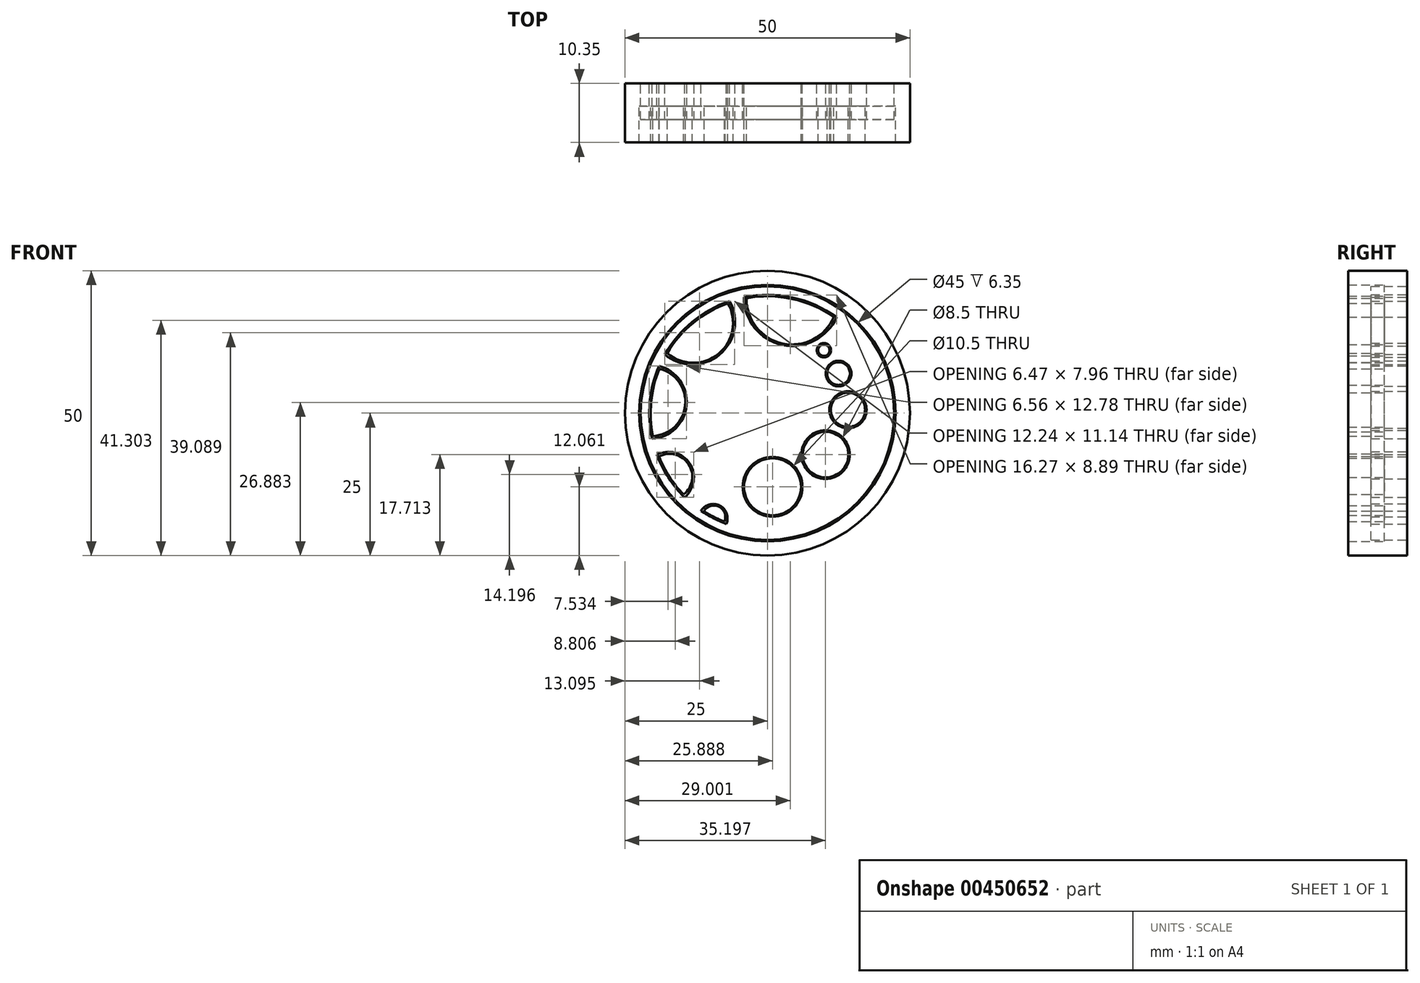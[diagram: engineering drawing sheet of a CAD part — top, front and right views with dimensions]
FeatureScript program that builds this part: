
annotation { "Feature Type Name" : "Feature", "Feature Type Description" : "" }
export const myFeature = defineFeature(function(context is Context, id is Id, definition is map)
    precondition{}
    {
        {
            var Q0;
            Q0=qCreatedBy(makeId("Front.planeOp"),FACE);
            var sketch = newSketch(context, id + "F0", { "sketchPlane" : qUnion([Q0])});
            skCircle(sketch, "E0", {"center": v(0, 0) * mm, "radius": 25 * mm});
            skCircle(sketch, "E1", {"center": v(0, 0) * mm, "radius": 20.5 * mm});
            skText(sketch, "E2", { "text": "BioE 123\n    SM", "fontName": "OpenSans-Bold.ttf"});
            skCircle(sketch, "E3", {"center": v(0.89, -12.94) * mm, "radius": 5 * mm});
            skCircle(sketch, "E4", {"center": v(10.2, -7.29) * mm, "radius": 4 * mm});
            skCircle(sketch, "E5", {"center": v(14.14, 0.57) * mm, "radius": 3 * mm});
            skCircle(sketch, "E6", {"center": v(12.48, 6.93) * mm, "radius": 2 * mm});
            skCircle(sketch, "E7", {"center": v(9.9, 11.03) * mm, "radius": 1 * mm});
            skCircle(sketch, "E8", {"center": v(0, 0) * mm, "radius": 22.5 * mm});
            skArc(sketch, "E9", {"start": v(-14.7, -14.29) * mm, "mid": v(-13.84, -8.99) * mm, "end": v(-19.03, -7.61) * mm});
            skArc(sketch, "E10", {"start": v(-20.1, -4.04) * mm, "mid": v(-14.43, 1.38) * mm, "end": v(-18.97, 7.78) * mm});
            skArc(sketch, "E11", {"start": v(-17.6, 10.52) * mm, "mid": v(-8.58, 10.42) * mm, "end": v(-6.95, 19.29) * mm});
            skArc(sketch, "E12", {"start": v(-3.68, 20.17) * mm, "mid": v(2.63, 12.22) * mm, "end": v(11.66, 16.86) * mm});
            skArc(sketch, "E13", {"start": v(-7.57, -19.05) * mm, "mid": v(-8.47, -16.45) * mm, "end": v(-11.12, -17.22) * mm});
            const initialGuessF0  = {"E2": [-0.01036, 0.0007, 1, 0, 0.00347]};
            skSetInitialGuess(sketch, initialGuessF0);
            skSolve(sketch);
        }
        {
            var Q0;
            Q0=qCreatedBy(makeId("Front.planeOp"),FACE);
            var sketch = newSketch(context, id + "F1", { "sketchPlane" : qUnion([Q0])});
            skCircle(sketch, "E14", {"center": v(0, 0) * mm, "radius": 25 * mm});
            skCircle(sketch, "E15", {"center": v(0, 0) * mm, "radius": 20.75 * mm});
            skText(sketch, "E16", { "text": "BioE 123\n    SM", "fontName": "OpenSans-Bold.ttf"});
            skCircle(sketch, "E17", {"center": v(0.89, -12.94) * mm, "radius": 5.25 * mm});
            skCircle(sketch, "E18", {"center": v(10.2, -7.29) * mm, "radius": 4.25 * mm});
            skCircle(sketch, "E19", {"center": v(14.14, 0.57) * mm, "radius": 3.25 * mm});
            skCircle(sketch, "E20", {"center": v(12.48, 6.93) * mm, "radius": 2.25 * mm});
            skCircle(sketch, "E21", {"center": v(9.9, 11.03) * mm, "radius": 1.25 * mm});
            skCircle(sketch, "E22", {"center": v(0, 0) * mm, "radius": 22.25 * mm});
            skArc(sketch, "E23", {"start": v(-14.56, -14.79) * mm, "mid": v(-13.63, -8.85) * mm, "end": v(-19.43, -7.28) * mm});
            skArc(sketch, "E24", {"start": v(-20.25, -4.5) * mm, "mid": v(-14.18, 1.36) * mm, "end": v(-19.03, 8.27) * mm});
            skArc(sketch, "E25", {"start": v(-18.02, 10.28) * mm, "mid": v(-8.42, 10.23) * mm, "end": v(-6.64, 19.66) * mm});
            skArc(sketch, "E26", {"start": v(-4.13, 20.33) * mm, "mid": v(2.58, 11.98) * mm, "end": v(12.13, 16.83) * mm});
            skArc(sketch, "E27", {"start": v(-7.22, -19.46) * mm, "mid": v(-8.36, -16.22) * mm, "end": v(-11.65, -17.17) * mm});
            const initialGuessF1  = {"E16": [-0.01036, 0.0007, 1, 0, 0.00347]};
            skSetInitialGuess(sketch, initialGuessF1);
            skSolve(sketch);
        }
        {
            var Q0;
            Q0=makeQuery(id+"F0.imprint","IMPRINT",FACE,{"disambiguationData":[TD([[makeQuery(id+"F0.imprint","IMPRINT",EDGE,{"derivedFrom":sQuery(id+"F0.wireOp",EDGE,"E6")}),1.0]])]});
            var Q1;
            Q1=makeQuery(id+"F0.imprint","IMPRINT",FACE,{"disambiguationData":[TD([[makeQuery(id+"F0.imprint","IMPRINT",EDGE,{"derivedFrom":sQuery(id+"F0.wireOp",EDGE,"E5")}),1.0]])]});
            var Q2;
            Q2=makeQuery(id+"F0.imprint","IMPRINT",FACE,{"disambiguationData":[TD([[makeQuery(id+"F0.imprint","IMPRINT",EDGE,{"derivedFrom":sQuery(id+"F0.wireOp",EDGE,"E4")}),1.0]])]});
            var Q3;
            Q3=makeQuery(id+"F0.imprint","IMPRINT",FACE,{"disambiguationData":[TD([[makeQuery(id+"F0.imprint","IMPRINT",EDGE,{"derivedFrom":sQuery(id+"F0.wireOp",EDGE,"E3")}),1.0]])]});
            var Q4;
            Q4=makeQuery(id+"F0.imprint","IMPRINT",FACE,{"disambiguationData":[TD([[makeQuery(id+"F0.imprint","IMPRINT",EDGE,{"derivedFrom":sQuery(id+"F0.wireOp",EDGE,"E2.sketch_text.stroke-0")}),1.0]])]});
            var Q5;
            Q5=makeQuery(id+"F0.imprint","IMPRINT",FACE,{"disambiguationData":[TD([[makeQuery(id+"F0.imprint","IMPRINT",EDGE,{"derivedFrom":sQuery(id+"F0.wireOp",EDGE,"E8")}),1.0]])]});
            var Q6;
            Q6=makeQuery(id+"F0.imprint","IMPRINT",FACE,{"disambiguationData":[TD([[makeQuery(id+"F0.imprint","IMPRINT",EDGE,{"derivedFrom":sQuery(id+"F0.wireOp",EDGE,"E0")}),1.0]])]});
            var Q7;
            {var subQ0=sQuery(id+"F0.wireOp",EDGE,"E13");Q7=makeQuery(id+"F0.imprint","IMPRINT",FACE,{"disambiguationData":[TD([[makeQuery(id+"F0.imprint","IMPRINT",EDGE,{"derivedFrom":subQ0}),1.0]])]});}
            var Q8;
            {var subQ0=sQuery(id+"F0.wireOp",EDGE,"E9");Q8=makeQuery(id+"F0.imprint","IMPRINT",FACE,{"disambiguationData":[TD([[makeQuery(id+"F0.imprint","IMPRINT",EDGE,{"derivedFrom":subQ0}),1.0]])]});}
            var Q9;
            {var subQ0=sQuery(id+"F0.wireOp",EDGE,"E10");Q9=makeQuery(id+"F0.imprint","IMPRINT",FACE,{"disambiguationData":[TD([[makeQuery(id+"F0.imprint","IMPRINT",EDGE,{"derivedFrom":subQ0}),1.0]])]});}
            var Q10;
            Q10=makeQuery(id+"F0.imprint","IMPRINT",FACE,{"disambiguationData":[TD([[makeQuery(id+"F0.imprint","IMPRINT",EDGE,{"derivedFrom":sQuery(id+"F0.wireOp",EDGE,"E2.sketch_text.stroke-125")}),-1.0]])]});
            var Q11;
            Q11=makeQuery(id+"F0.imprint","IMPRINT",FACE,{"disambiguationData":[TD([[makeQuery(id+"F0.imprint","IMPRINT",EDGE,{"derivedFrom":sQuery(id+"F0.wireOp",EDGE,"E2.sketch_text.stroke-153")}),-1.0]])]});
            var Q12;
            {var subQ0=sQuery(id+"F0.wireOp",EDGE,"E11");Q12=makeQuery(id+"F0.imprint","IMPRINT",FACE,{"disambiguationData":[TD([[makeQuery(id+"F0.imprint","IMPRINT",EDGE,{"derivedFrom":subQ0}),1.0]])]});}
            var Q13;
            {var subQ0=sQuery(id+"F0.wireOp",EDGE,"E12");Q13=makeQuery(id+"F0.imprint","IMPRINT",FACE,{"disambiguationData":[TD([[makeQuery(id+"F0.imprint","IMPRINT",EDGE,{"derivedFrom":subQ0}),1.0]])]});}
            var Q14;
            Q14=makeQuery(id+"F0.imprint","IMPRINT",FACE,{"disambiguationData":[TD([[makeQuery(id+"F0.imprint","IMPRINT",EDGE,{"derivedFrom":sQuery(id+"F0.wireOp",EDGE,"E2.sketch_text.stroke-0")}),-1.0]])]});
            var Q15;
            Q15=makeQuery(id+"F0.imprint","IMPRINT",FACE,{"disambiguationData":[TD([[makeQuery(id+"F0.imprint","IMPRINT",EDGE,{"derivedFrom":sQuery(id+"F0.wireOp",EDGE,"E2.sketch_text.stroke-12")}),1.0]])]});
            var Q16;
            Q16=makeQuery(id+"F0.imprint","IMPRINT",FACE,{"disambiguationData":[TD([[makeQuery(id+"F0.imprint","IMPRINT",EDGE,{"derivedFrom":sQuery(id+"F0.wireOp",EDGE,"E2.sketch_text.stroke-19")}),1.0]])]});
            var Q17;
            Q17=makeQuery(id+"F0.imprint","IMPRINT",FACE,{"disambiguationData":[TD([[makeQuery(id+"F0.imprint","IMPRINT",EDGE,{"derivedFrom":sQuery(id+"F0.wireOp",EDGE,"E2.sketch_text.stroke-30")}),-1.0]])]});
            var Q18;
            Q18=makeQuery(id+"F0.imprint","IMPRINT",FACE,{"disambiguationData":[TD([[makeQuery(id+"F0.imprint","IMPRINT",EDGE,{"derivedFrom":sQuery(id+"F0.wireOp",EDGE,"E2.sketch_text.stroke-25")}),-1.0]])]});
            var Q19;
            Q19=makeQuery(id+"F0.imprint","IMPRINT",FACE,{"disambiguationData":[TD([[makeQuery(id+"F0.imprint","IMPRINT",EDGE,{"derivedFrom":sQuery(id+"F0.wireOp",EDGE,"E2.sketch_text.stroke-34")}),-1.0]])]});
            var Q20;
            Q20=makeQuery(id+"F0.imprint","IMPRINT",FACE,{"disambiguationData":[TD([[makeQuery(id+"F0.imprint","IMPRINT",EDGE,{"derivedFrom":sQuery(id+"F0.wireOp",EDGE,"E2.sketch_text.stroke-52")}),-1.0]])]});
            var Q21;
            Q21=makeQuery(id+"F0.imprint","IMPRINT",FACE,{"disambiguationData":[TD([[makeQuery(id+"F0.imprint","IMPRINT",EDGE,{"derivedFrom":sQuery(id+"F0.wireOp",EDGE,"E2.sketch_text.stroke-34")}),1.0]])]});
            var Q22;
            Q22=makeQuery(id+"F0.imprint","IMPRINT",FACE,{"disambiguationData":[TD([[makeQuery(id+"F0.imprint","IMPRINT",EDGE,{"derivedFrom":sQuery(id+"F0.wireOp",EDGE,"E2.sketch_text.stroke-64")}),-1.0]])]});
            var Q23;
            Q23=makeQuery(id+"F0.imprint","IMPRINT",FACE,{"disambiguationData":[TD([[makeQuery(id+"F0.imprint","IMPRINT",EDGE,{"derivedFrom":sQuery(id+"F0.wireOp",EDGE,"E2.sketch_text.stroke-74")}),-1.0]])]});
            var Q24;
            Q24=makeQuery(id+"F0.imprint","IMPRINT",FACE,{"disambiguationData":[TD([[makeQuery(id+"F0.imprint","IMPRINT",EDGE,{"derivedFrom":sQuery(id+"F0.wireOp",EDGE,"E7")}),1.0]])]});
            var Q25;
            Q25=makeQuery(id+"F0.imprint","IMPRINT",FACE,{"disambiguationData":[TD([[makeQuery(id+"F0.imprint","IMPRINT",EDGE,{"derivedFrom":sQuery(id+"F0.wireOp",EDGE,"E2.sketch_text.stroke-98")}),-1.0]])]});
            extrude(context, id + "F2", {"entities" : qUnion([Q0, Q1, Q2, Q3, Q4, Q5, Q6, Q7, Q8, Q9, Q10, Q11, Q12, Q13, Q14, Q15, Q16, Q17, Q18, Q19, Q20, Q21, Q22, Q23, Q24, Q25]), "depth" : 4 * mm});
        }
        {
            var Q0;
            Q0=makeQuery(id+"F0.imprint","IMPRINT",FACE,{"disambiguationData":[TD([[makeQuery(id+"F0.imprint","IMPRINT",EDGE,{"derivedFrom":sQuery(id+"F0.wireOp",EDGE,"E0")}),1.0]])]});
            extrude(context, id + "F3", {"entities" : qUnion([Q0]), "operationType" : NewBodyOperationType.ADD, "depth" : 10.35 * mm});
        }
        {
            var Q0;
            {var subQ0=sQuery(id+"F0.wireOp",EDGE,"E13");Q0=makeQuery(id+"F0.imprint","IMPRINT",FACE,{"disambiguationData":[TD([[makeQuery(id+"F0.imprint","IMPRINT",EDGE,{"derivedFrom":subQ0}),1.0]])]});}
            var Q1;
            {var subQ0=sQuery(id+"F0.wireOp",EDGE,"E9");Q1=makeQuery(id+"F0.imprint","IMPRINT",FACE,{"disambiguationData":[TD([[makeQuery(id+"F0.imprint","IMPRINT",EDGE,{"derivedFrom":subQ0}),1.0]])]});}
            var Q2;
            {var subQ0=sQuery(id+"F0.wireOp",EDGE,"E10");Q2=makeQuery(id+"F0.imprint","IMPRINT",FACE,{"disambiguationData":[TD([[makeQuery(id+"F0.imprint","IMPRINT",EDGE,{"derivedFrom":subQ0}),1.0]])]});}
            var Q3;
            {var subQ0=sQuery(id+"F0.wireOp",EDGE,"E11");Q3=makeQuery(id+"F0.imprint","IMPRINT",FACE,{"disambiguationData":[TD([[makeQuery(id+"F0.imprint","IMPRINT",EDGE,{"derivedFrom":subQ0}),1.0]])]});}
            var Q4;
            {var subQ0=sQuery(id+"F0.wireOp",EDGE,"E12");Q4=makeQuery(id+"F0.imprint","IMPRINT",FACE,{"disambiguationData":[TD([[makeQuery(id+"F0.imprint","IMPRINT",EDGE,{"derivedFrom":subQ0}),1.0]])]});}
            var Q5;
            Q5=makeQuery(id+"F0.imprint","IMPRINT",FACE,{"disambiguationData":[TD([[makeQuery(id+"F0.imprint","IMPRINT",EDGE,{"derivedFrom":sQuery(id+"F0.wireOp",EDGE,"E7")}),1.0]])]});
            var Q6;
            Q6=makeQuery(id+"F0.imprint","IMPRINT",FACE,{"disambiguationData":[TD([[makeQuery(id+"F0.imprint","IMPRINT",EDGE,{"derivedFrom":sQuery(id+"F0.wireOp",EDGE,"E6")}),1.0]])]});
            var Q7;
            Q7=makeQuery(id+"F0.imprint","IMPRINT",FACE,{"disambiguationData":[TD([[makeQuery(id+"F0.imprint","IMPRINT",EDGE,{"derivedFrom":sQuery(id+"F0.wireOp",EDGE,"E5")}),1.0]])]});
            var Q8;
            Q8=makeQuery(id+"F0.imprint","IMPRINT",FACE,{"disambiguationData":[TD([[makeQuery(id+"F0.imprint","IMPRINT",EDGE,{"derivedFrom":sQuery(id+"F0.wireOp",EDGE,"E4")}),1.0]])]});
            var Q9;
            Q9=makeQuery(id+"F0.imprint","IMPRINT",FACE,{"disambiguationData":[TD([[makeQuery(id+"F0.imprint","IMPRINT",EDGE,{"derivedFrom":sQuery(id+"F0.wireOp",EDGE,"E3")}),1.0]])]});
            var Q10;
            Q10=makeQuery(id+"F3.opExtrude","CAP_FACE",FACE,{"disambiguationData":[OSD([sQuery(id+"F0.wireOp",EDGE,"E0"),sQuery(id+"F0.wireOp",EDGE,"E8")])],"isStart":false});
            extrude(context, id + "F4", {"entities" : qUnion([Q0, Q1, Q2, Q3, Q4, Q5, Q6, Q7, Q8, Q9]), "operationType" : NewBodyOperationType.ADD, "endBound" : BoundingType.UP_TO_SURFACE, "endBoundEntityFace" : qUnion([Q10]), "depth" : 25.4 * mm});
        }
        {
            var Q0;
            Q0=makeQuery(id+"F1.imprint","IMPRINT",FACE,{"disambiguationData":[TD([[makeQuery(id+"F1.imprint","IMPRINT",EDGE,{"derivedFrom":sQuery(id+"F1.wireOp",EDGE,"E22")}),1.0]])]});
            var Q1;
            Q1=makeQuery(id+"F1.imprint","IMPRINT",FACE,{"disambiguationData":[TD([[makeQuery(id+"F1.imprint","IMPRINT",EDGE,{"derivedFrom":sQuery(id+"F1.wireOp",EDGE,"E16.sketch_text.stroke-98")}),-1.0]])]});
            var Q2;
            Q2=makeQuery(id+"F1.imprint","IMPRINT",FACE,{"disambiguationData":[TD([[makeQuery(id+"F1.imprint","IMPRINT",EDGE,{"derivedFrom":sQuery(id+"F1.wireOp",EDGE,"E16.sketch_text.stroke-74")}),-1.0]])]});
            var Q3;
            Q3=makeQuery(id+"F1.imprint","IMPRINT",FACE,{"disambiguationData":[TD([[makeQuery(id+"F1.imprint","IMPRINT",EDGE,{"derivedFrom":sQuery(id+"F1.wireOp",EDGE,"E16.sketch_text.stroke-64")}),-1.0]])]});
            var Q4;
            Q4=makeQuery(id+"F1.imprint","IMPRINT",FACE,{"disambiguationData":[TD([[makeQuery(id+"F1.imprint","IMPRINT",EDGE,{"derivedFrom":sQuery(id+"F1.wireOp",EDGE,"E16.sketch_text.stroke-52")}),-1.0]])]});
            var Q5;
            Q5=makeQuery(id+"F1.imprint","IMPRINT",FACE,{"disambiguationData":[TD([[makeQuery(id+"F1.imprint","IMPRINT",EDGE,{"derivedFrom":sQuery(id+"F1.wireOp",EDGE,"E16.sketch_text.stroke-34")}),-1.0]])]});
            var Q6;
            Q6=makeQuery(id+"F1.imprint","IMPRINT",FACE,{"disambiguationData":[TD([[makeQuery(id+"F1.imprint","IMPRINT",EDGE,{"derivedFrom":sQuery(id+"F1.wireOp",EDGE,"E16.sketch_text.stroke-34")}),1.0]])]});
            var Q7;
            Q7=makeQuery(id+"F1.imprint","IMPRINT",FACE,{"disambiguationData":[TD([[makeQuery(id+"F1.imprint","IMPRINT",EDGE,{"derivedFrom":sQuery(id+"F1.wireOp",EDGE,"E16.sketch_text.stroke-30")}),-1.0]])]});
            var Q8;
            Q8=makeQuery(id+"F1.imprint","IMPRINT",FACE,{"disambiguationData":[TD([[makeQuery(id+"F1.imprint","IMPRINT",EDGE,{"derivedFrom":sQuery(id+"F1.wireOp",EDGE,"E16.sketch_text.stroke-25")}),-1.0]])]});
            var Q9;
            Q9=makeQuery(id+"F1.imprint","IMPRINT",FACE,{"disambiguationData":[TD([[makeQuery(id+"F1.imprint","IMPRINT",EDGE,{"derivedFrom":sQuery(id+"F1.wireOp",EDGE,"E16.sketch_text.stroke-0")}),-1.0]])]});
            var Q10;
            Q10=makeQuery(id+"F1.imprint","IMPRINT",FACE,{"disambiguationData":[TD([[makeQuery(id+"F1.imprint","IMPRINT",EDGE,{"derivedFrom":sQuery(id+"F1.wireOp",EDGE,"E16.sketch_text.stroke-12")}),1.0]])]});
            var Q11;
            Q11=makeQuery(id+"F1.imprint","IMPRINT",FACE,{"disambiguationData":[TD([[makeQuery(id+"F1.imprint","IMPRINT",EDGE,{"derivedFrom":sQuery(id+"F1.wireOp",EDGE,"E16.sketch_text.stroke-19")}),1.0]])]});
            var Q12;
            Q12=makeQuery(id+"F1.imprint","IMPRINT",FACE,{"disambiguationData":[TD([[makeQuery(id+"F1.imprint","IMPRINT",EDGE,{"derivedFrom":sQuery(id+"F1.wireOp",EDGE,"E16.sketch_text.stroke-125")}),-1.0]])]});
            var Q13;
            Q13=makeQuery(id+"F1.imprint","IMPRINT",FACE,{"disambiguationData":[TD([[makeQuery(id+"F1.imprint","IMPRINT",EDGE,{"derivedFrom":sQuery(id+"F1.wireOp",EDGE,"E16.sketch_text.stroke-153")}),-1.0]])]});
            var Q14;
            Q14=makeQuery(id+"F1.imprint","IMPRINT",FACE,{"disambiguationData":[TD([[makeQuery(id+"F1.imprint","IMPRINT",EDGE,{"derivedFrom":sQuery(id+"F1.wireOp",EDGE,"E16.sketch_text.stroke-0")}),1.0]])]});
            extrude(context, id + "F5", {"entities" : qUnion([Q0, Q1, Q2, Q3, Q4, Q5, Q6, Q7, Q8, Q9, Q10, Q11, Q12, Q13, Q14]), "depth" : 6.35 * mm});
        }
    });
